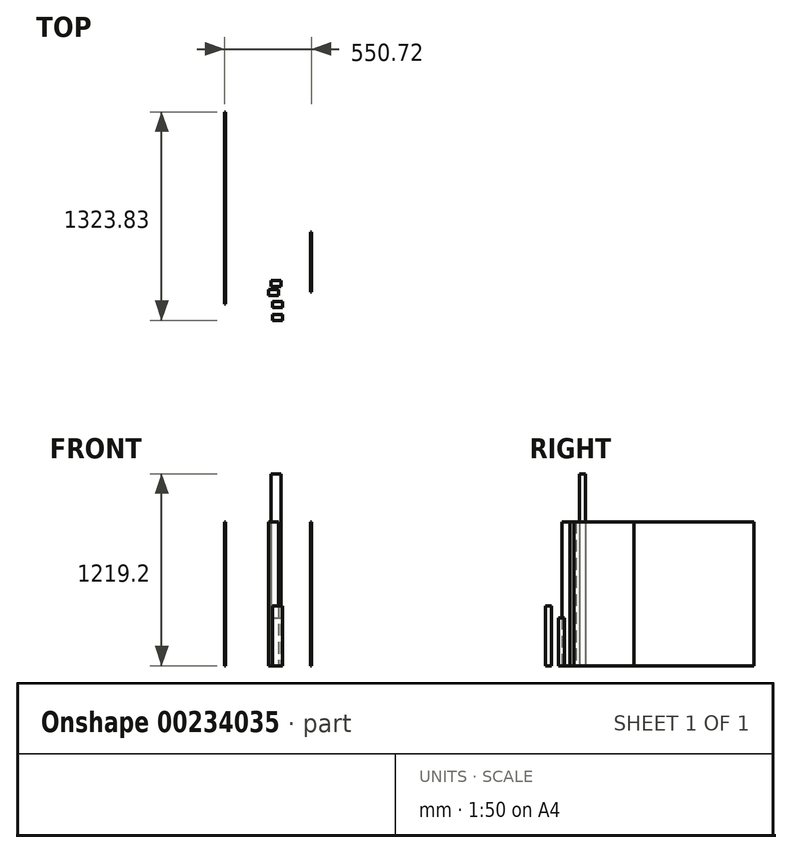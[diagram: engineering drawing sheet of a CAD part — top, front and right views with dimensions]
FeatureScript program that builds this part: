
annotation { "Feature Type Name" : "Feature", "Feature Type Description" : "" }
export const myFeature = defineFeature(function(context is Context, id is Id, definition is map)
    precondition{}
    {
        {
            var Q0;
            Q0=qCreatedBy(makeId("Top.planeOp"),FACE);
            var sketch = newSketch(context, id + "F0", { "sketchPlane" : qUnion([Q0])});
            skLineSegment(sketch, "E0.bottom", {"start": v(-29.06, 15.42) * mm, "end": v(34.44, 15.42) * mm});
            skLineSegment(sketch, "E0.top", {"start": v(-29.06, -22.68) * mm, "end": v(34.44, -22.68) * mm});
            skLineSegment(sketch, "E0.left", {"start": v(-29.06, 15.42) * mm, "end": v(-29.06, -22.68) * mm});
            skLineSegment(sketch, "E0.right", {"start": v(34.44, 15.42) * mm, "end": v(34.44, -22.68) * mm});
            skSolve(sketch);
        }
        {
            var Q0;
            Q0 = qSketchRegion(id + "F0", true);
            extrude(context, id + "F1", {"entities" : qUnion([Q0]), "depth" : 914.4 * mm});
        }
        {
            var Q0;
            Q0=qCreatedBy(makeId("Top.planeOp"),FACE);
            var sketch = newSketch(context, id + "F2", { "sketchPlane" : qUnion([Q0])});
            skLineSegment(sketch, "E1.bottom", {"start": v(-12.9, 74.75) * mm, "end": v(50.6, 74.75) * mm});
            skLineSegment(sketch, "E1.top", {"start": v(-12.9, 36.65) * mm, "end": v(50.6, 36.65) * mm});
            skLineSegment(sketch, "E1.left", {"start": v(-12.9, 74.75) * mm, "end": v(-12.9, 36.65) * mm});
            skLineSegment(sketch, "E1.right", {"start": v(50.6, 74.75) * mm, "end": v(50.6, 36.65) * mm});
            skSolve(sketch);
        }
        {
            var Q0;
            Q0 = qSketchRegion(id + "F2", true);
            extrude(context, id + "F3", {"entities" : qUnion([Q0]), "depth" : 1219.2 * mm});
        }
        {
            var Q0;
            Q0=qCreatedBy(makeId("Top.planeOp"),FACE);
            var sketch = newSketch(context, id + "F4", { "sketchPlane" : qUnion([Q0])});
            skLineSegment(sketch, "E2.bottom", {"start": v(-4.42, -60.35) * mm, "end": v(59.08, -60.35) * mm});
            skLineSegment(sketch, "E2.top", {"start": v(-4.42, -98.45) * mm, "end": v(59.08, -98.45) * mm});
            skLineSegment(sketch, "E2.left", {"start": v(-4.42, -60.35) * mm, "end": v(-4.42, -98.45) * mm});
            skLineSegment(sketch, "E2.right", {"start": v(59.08, -60.35) * mm, "end": v(59.08, -98.45) * mm});
            skSolve(sketch);
        }
        {
            var Q0;
            Q0 = qSketchRegion(id + "F4", true);
            extrude(context, id + "F5", {"entities" : qUnion([Q0]), "depth" : 304.8 * mm});
        }
        {
            var Q0;
            Q0=qCreatedBy(makeId("Top.planeOp"),FACE);
            var sketch = newSketch(context, id + "F6", { "sketchPlane" : qUnion([Q0])});
            skLineSegment(sketch, "E3.bottom", {"start": v(-4.7, -141.1) * mm, "end": v(58.8, -141.1) * mm});
            skLineSegment(sketch, "E3.top", {"start": v(-4.7, -179.2) * mm, "end": v(58.8, -179.2) * mm});
            skLineSegment(sketch, "E3.left", {"start": v(-4.7, -141.1) * mm, "end": v(-4.7, -179.2) * mm});
            skLineSegment(sketch, "E3.right", {"start": v(58.8, -141.1) * mm, "end": v(58.8, -179.2) * mm});
            skSolve(sketch);
        }
        {
            var Q0;
            Q0=makeQuery(id+"F6.imprint","IMPRINT",FACE,{"disambiguationData":[TD([[makeQuery(id+"F6.imprint","IMPRINT",EDGE,{"derivedFrom":sQuery(id+"F6.wireOp",EDGE,"E3.bottom")}),-1.0]])]});
            extrude(context, id + "F7", {"entities" : qUnion([Q0]), "depth" : 381 * mm});
        }
        {
            var Q0;
            Q0=qCreatedBy(makeId("Top.planeOp"),FACE);
            var sketch = newSketch(context, id + "F8", { "sketchPlane" : qUnion([Q0])});
            skLineSegment(sketch, "E4.bottom", {"start": v(-307.44, 1144.62) * mm, "end": v(-301.09, 1144.62) * mm});
            skLineSegment(sketch, "E4.top", {"start": v(-307.44, -74.58) * mm, "end": v(-301.09, -74.58) * mm});
            skLineSegment(sketch, "E4.left", {"start": v(-307.44, 1144.62) * mm, "end": v(-307.44, -74.58) * mm});
            skLineSegment(sketch, "E4.right", {"start": v(-301.09, 1144.62) * mm, "end": v(-301.09, -74.58) * mm});
            skSolve(sketch);
        }
        {
            var Q0;
            Q0 = qSketchRegion(id + "F8", true);
            extrude(context, id + "F9", {"entities" : qUnion([Q0]), "depth" : 914.4 * mm});
        }
        {
            var Q0;
            Q0=qCreatedBy(makeId("Top.planeOp"),FACE);
            var sketch = newSketch(context, id + "F10", { "sketchPlane" : qUnion([Q0])});
            skLineSegment(sketch, "E5.bottom", {"start": v(236.93, 381.03) * mm, "end": v(243.28, 381.03) * mm});
            skLineSegment(sketch, "E5.top", {"start": v(236.93, 0.03) * mm, "end": v(243.28, 0.03) * mm});
            skLineSegment(sketch, "E5.left", {"start": v(236.93, 381.03) * mm, "end": v(236.93, 0.03) * mm});
            skLineSegment(sketch, "E5.right", {"start": v(243.28, 381.03) * mm, "end": v(243.28, 0.03) * mm});
            skSolve(sketch);
        }
        {
            var Q0;
            Q0 = qSketchRegion(id + "F10", true);
            extrude(context, id + "F11", {"entities" : qUnion([Q0]), "depth" : 914.4 * mm});
        }
    });
